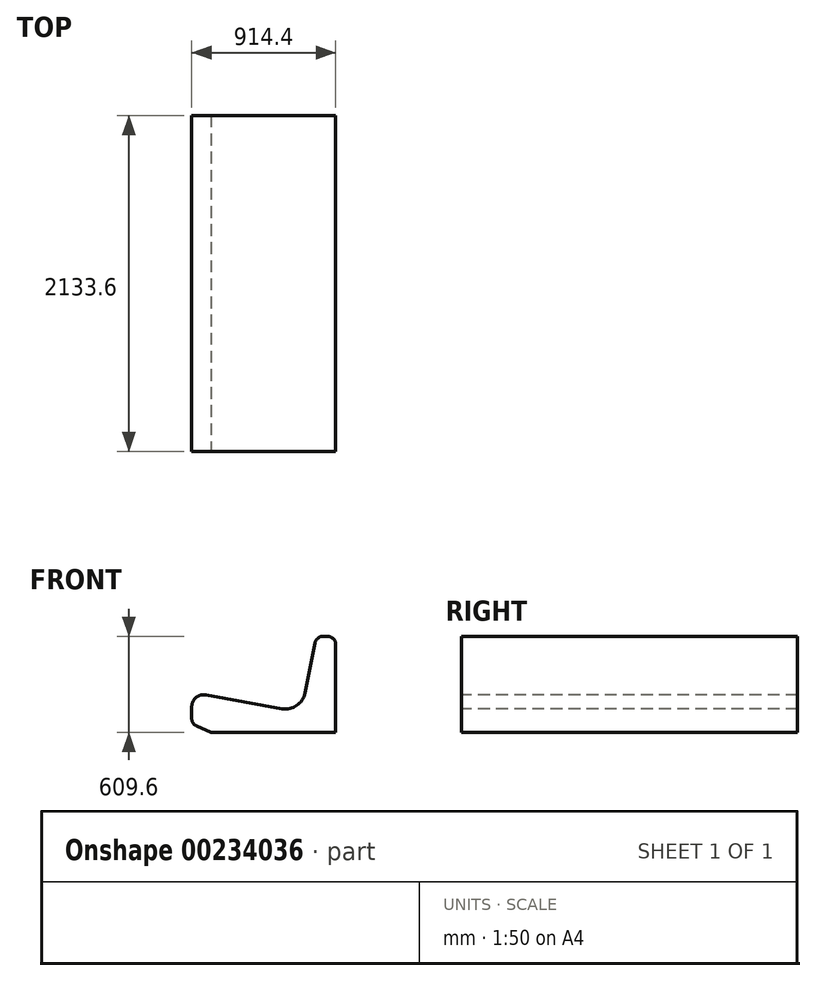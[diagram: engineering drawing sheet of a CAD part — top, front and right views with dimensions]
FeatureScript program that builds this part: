
annotation { "Feature Type Name" : "Feature", "Feature Type Description" : "" }
export const myFeature = defineFeature(function(context is Context, id is Id, definition is map)
    precondition{}
    {
        {
            var Q0;
            Q0=qCreatedBy(makeId("Top.planeOp"),FACE);
            var sketch = newSketch(context, id + "F0", { "sketchPlane" : qUnion([Q0])});
            skLineSegment(sketch, "E0.bottom", {"start": v(-1606.51, 1115.13) * mm, "end": v(1466.89, 1115.13) * mm});
            skLineSegment(sketch, "E0.top", {"start": v(-1606.51, -1323.27) * mm, "end": v(1466.89, -1323.27) * mm});
            skLineSegment(sketch, "E0.left", {"start": v(-1606.51, 1115.13) * mm, "end": v(-1606.51, -1323.27) * mm});
            skLineSegment(sketch, "E0.right", {"start": v(1466.89, 1115.13) * mm, "end": v(1466.89, -1323.27) * mm});
            skLineSegment(sketch, "E1.bottom", {"start": v(-1657.31, 1165.93) * mm, "end": v(1517.69, 1165.93) * mm});
            skLineSegment(sketch, "E1.top", {"start": v(-1657.31, -1374.07) * mm, "end": v(1517.69, -1374.07) * mm});
            skLineSegment(sketch, "E1.left", {"start": v(-1657.31, 1165.93) * mm, "end": v(-1657.31, -1374.07) * mm});
            skLineSegment(sketch, "E1.right", {"start": v(1517.69, 1165.93) * mm, "end": v(1517.69, -1374.07) * mm});
            skSolve(sketch);
        }
        {
            var Q0;
            Q0=makeQuery(id+"F0.imprint","IMPRINT",FACE,{"disambiguationData":[TD([[makeQuery(id+"F0.imprint","IMPRINT",EDGE,{"derivedFrom":sQuery(id+"F0.wireOp",EDGE,"E0.bottom")}),1.0]])]});
            extrude(context, id + "F1", {"entities" : qUnion([Q0]), "depth" : 2438.4 * mm});
        }
        {
            var Q0;
            Q0=makeQuery(id+"F1.opExtrude","SWEPT_FACE",FACE,{"disambiguationData":[OSD([sQuery(id+"F0.wireOp",EDGE,"E1.top")])]});
            var sketch = newSketch(context, id + "F2", { "sketchPlane" : qUnion([Q0])});
            skLineSegment(sketch, "E2.bottom", {"start": v(-946.11, 0) * mm, "end": v(476.29, 0) * mm});
            skLineSegment(sketch, "E2.top", {"start": v(-946.11, 2006.6) * mm, "end": v(476.29, 2006.6) * mm});
            skLineSegment(sketch, "E2.left", {"start": v(-946.11, 0) * mm, "end": v(-946.11, 2006.6) * mm});
            skLineSegment(sketch, "E2.right", {"start": v(476.29, 0) * mm, "end": v(476.29, 2006.6) * mm});
            skSolve(sketch);
        }
        {
            var Q0;
            Q0 = qSketchRegion(id + "F2", true);
            extrude(context, id + "F3", {"entities" : qUnion([Q0]), "operationType" : NewBodyOperationType.REMOVE, "endBound" : BoundingType.UP_TO_NEXT, "oppositeDirection" : true, "depth" : 25.4 * mm});
        }
        {
            var Q0;
            Q0=makeQuery(id+"F1.opExtrude","SWEPT_FACE",FACE,{"disambiguationData":[OSD([sQuery(id+"F0.wireOp",EDGE,"E0.bottom")])]});
            var sketch = newSketch(context, id + "F4", { "sketchPlane" : qUnion([Q0])});
            skLineSegment(sketch, "E3.bottom", {"start": v(-1657.31, 711.2) * mm, "end": v(781.09, 711.2) * mm});
            skLineSegment(sketch, "E3.top", {"start": v(-1657.31, 2082.8) * mm, "end": v(781.09, 2082.8) * mm});
            skLineSegment(sketch, "E3.left", {"start": v(-1657.31, 711.2) * mm, "end": v(-1657.31, 2082.8) * mm});
            skLineSegment(sketch, "E3.right", {"start": v(781.09, 711.2) * mm, "end": v(781.09, 2082.8) * mm});
            skSolve(sketch);
        }
        {
            var Q0;
            Q0 = qSketchRegion(id + "F4", true);
            extrude(context, id + "F5", {"entities" : qUnion([Q0]), "operationType" : NewBodyOperationType.REMOVE, "endBound" : BoundingType.UP_TO_NEXT, "oppositeDirection" : true, "depth" : 25.4 * mm});
        }
        {
            var Q0;
            Q0=qCreatedBy(makeId("Top.planeOp"),FACE);
            var sketch = newSketch(context, id + "F6", { "sketchPlane" : qUnion([Q0])});
            skLineSegment(sketch, "E4.bottom", {"start": v(-869.91, 1096.08) * mm, "end": v(374.69, 1096.08) * mm});
            skLineSegment(sketch, "E4.top", {"start": v(-869.91, 867.48) * mm, "end": v(374.69, 867.48) * mm});
            skLineSegment(sketch, "E4.left", {"start": v(-869.91, 1096.08) * mm, "end": v(-869.91, 867.48) * mm});
            skLineSegment(sketch, "E4.right", {"start": v(374.69, 1096.08) * mm, "end": v(374.69, 867.48) * mm});
            skSolve(sketch);
        }
        {
            var Q0;
            Q0=makeQuery(id+"F6.imprint","IMPRINT",FACE,{"disambiguationData":[TD([[makeQuery(id+"F6.imprint","IMPRINT",EDGE,{"derivedFrom":sQuery(id+"F6.wireOp",EDGE,"E4.bottom")}),-1.0]])]});
            extrude(context, id + "F7", {"entities" : qUnion([Q0]), "operationType" : NewBodyOperationType.ADD, "depth" : 508 * mm});
        }
        {
            var Q0;
            Q0=qCreatedBy(makeId("Top.planeOp"),FACE);
            var sketch = newSketch(context, id + "F8", { "sketchPlane" : qUnion([Q0])});
            skLineSegment(sketch, "E5.bottom", {"start": v(-1530.31, 1077.03) * mm, "end": v(-1022.31, 1077.03) * mm});
            skLineSegment(sketch, "E5.top", {"start": v(-1530.31, 518.23) * mm, "end": v(-1022.31, 518.23) * mm});
            skLineSegment(sketch, "E5.left", {"start": v(-1530.31, 1077.03) * mm, "end": v(-1530.31, 518.23) * mm});
            skLineSegment(sketch, "E5.right", {"start": v(-1022.31, 1077.03) * mm, "end": v(-1022.31, 518.23) * mm});
            skSolve(sketch);
        }
        {
            var Q0;
            Q0=makeQuery(id+"F8.imprint","IMPRINT",FACE,{"disambiguationData":[TD([[makeQuery(id+"F8.imprint","IMPRINT",EDGE,{"derivedFrom":sQuery(id+"F8.wireOp",EDGE,"E5.bottom")}),-1.0]])]});
            extrude(context, id + "F9", {"entities" : qUnion([Q0]), "operationType" : NewBodyOperationType.ADD, "depth" : 838.2 * mm});
        }
        {
            var Q0;
            Q0=makeQuery(id+"F7.opExtrude","SWEPT_FACE",FACE,{"disambiguationData":[OSD([sQuery(id+"F6.wireOp",EDGE,"E4.top")])]});
            var sketch = newSketch(context, id + "F10", { "sketchPlane" : qUnion([Q0])});
            skLineSegment(sketch, "E6.bottom", {"start": v(-869.91, 508) * mm, "end": v(-717.51, 508) * mm});
            skLineSegment(sketch, "E6.top", {"start": v(-869.91, 254) * mm, "end": v(-717.51, 254) * mm});
            skLineSegment(sketch, "E6.left", {"start": v(-869.91, 508) * mm, "end": v(-869.91, 254) * mm});
            skLineSegment(sketch, "E6.right", {"start": v(-717.51, 508) * mm, "end": v(-717.51, 254) * mm});
            skSolve(sketch);
        }
        {
            var Q0;
            Q0 = qSketchRegion(id + "F10", true);
            extrude(context, id + "F11", {"entities" : qUnion([Q0]), "operationType" : NewBodyOperationType.REMOVE, "endBound" : BoundingType.UP_TO_NEXT, "oppositeDirection" : true, "depth" : 25.4 * mm});
        }
        {
            var Q0;
            Q0=qCreatedBy(makeId("Top.planeOp"),FACE);
            var sketch = newSketch(context, id + "F12", { "sketchPlane" : qUnion([Q0])});
            skLineSegment(sketch, "E7.bottom", {"start": v(476.29, 962.73) * mm, "end": v(1390.69, 962.73) * mm});
            skLineSegment(sketch, "E7.top", {"start": v(476.29, -1170.87) * mm, "end": v(1390.69, -1170.87) * mm});
            skLineSegment(sketch, "E7.left", {"start": v(476.29, 962.73) * mm, "end": v(476.29, -1170.87) * mm});
            skLineSegment(sketch, "E7.right", {"start": v(1390.69, 962.73) * mm, "end": v(1390.69, -1170.87) * mm});
            skSolve(sketch);
        }
        {
            var Q0;
            Q0 = qSketchRegion(id + "F12", true);
            extrude(context, id + "F13", {"entities" : qUnion([Q0]), "depth" : 609.6 * mm});
        }
        {
            var Q0;
            Q0=makeQuery(id+"F13.opExtrude","SWEPT_FACE",FACE,{"disambiguationData":[OSD([sQuery(id+"F12.wireOp",EDGE,"E7.top")])]});
            var sketch = newSketch(context, id + "F14", { "sketchPlane" : qUnion([Q0])});
            skLineSegment(sketch, "E8", {"start": v(1258.9, 568.65) * mm, "end": v(1196.1, 250.89) * mm});
            skLineSegment(sketch, "E9", {"start": v(1048.82, 150.56) * mm, "end": v(566.1, 238.2) * mm});
            skLineSegment(sketch, "E10", {"start": v(476.29, 163.23) * mm, "end": v(476.29, 86.78) * mm});
            skLineSegment(sketch, "E11", {"start": v(506.7, 40.25) * mm, "end": v(598.56, 0) * mm});
            skLineSegment(sketch, "E12", {"start": v(598.56, 0) * mm, "end": v(1390.69, 0) * mm});
            skLineSegment(sketch, "E13", {"start": v(1390.69, 0) * mm, "end": v(1390.69, 558.8) * mm});
            skLineSegment(sketch, "E14", {"start": v(1339.89, 609.6) * mm, "end": v(1308.73, 609.6) * mm});
            skPoint(sketch, "E15.visualSharp", {"position": v(476.29, 254.5) * mm});
            skArc(sketch, "E15.filletArc", {"start": v(566.1, 238.2) * mm, "mid": v(503.65, 221.72) * mm, "end": v(476.29, 163.23) * mm});
            skPoint(sketch, "E16.visualSharp", {"position": v(476.29, 53.57) * mm});
            skArc(sketch, "E16.filletArc", {"start": v(476.29, 86.78) * mm, "mid": v(484.56, 58.98) * mm, "end": v(506.7, 40.25) * mm});
            skPoint(sketch, "E17.visualSharp", {"position": v(1171.85, 128.22) * mm});
            skArc(sketch, "E17.filletArc", {"start": v(1048.82, 150.56) * mm, "mid": v(1143, 170.55) * mm, "end": v(1196.1, 250.89) * mm});
            skPoint(sketch, "E18.visualSharp", {"position": v(1267, 609.6) * mm});
            skArc(sketch, "E18.filletArc", {"start": v(1308.73, 609.6) * mm, "mid": v(1276.48, 598.05) * mm, "end": v(1258.9, 568.65) * mm});
            skPoint(sketch, "E19.visualSharp", {"position": v(1390.69, 609.6) * mm});
            skArc(sketch, "E19.filletArc", {"start": v(1390.69, 558.8) * mm, "mid": v(1375.8, 594.72) * mm, "end": v(1339.89, 609.6) * mm});
            skSolve(sketch);
        }
        {
            var Q0;
            Q0=makeQuery(id+"F14.imprint","IMPRINT",FACE,{"disambiguationData":[TD([[makeQuery(id+"F14.imprint","IMPRINT",EDGE,{"derivedFrom":sQuery(id+"F14.wireOp",EDGE,"E8")}),1.0]])]});
            extrude(context, id + "F15", {"entities" : qUnion([Q0]), "operationType" : NewBodyOperationType.INTERSECT, "endBound" : BoundingType.UP_TO_NEXT, "oppositeDirection" : true, "depth" : 25.4 * mm});
        }
    });
